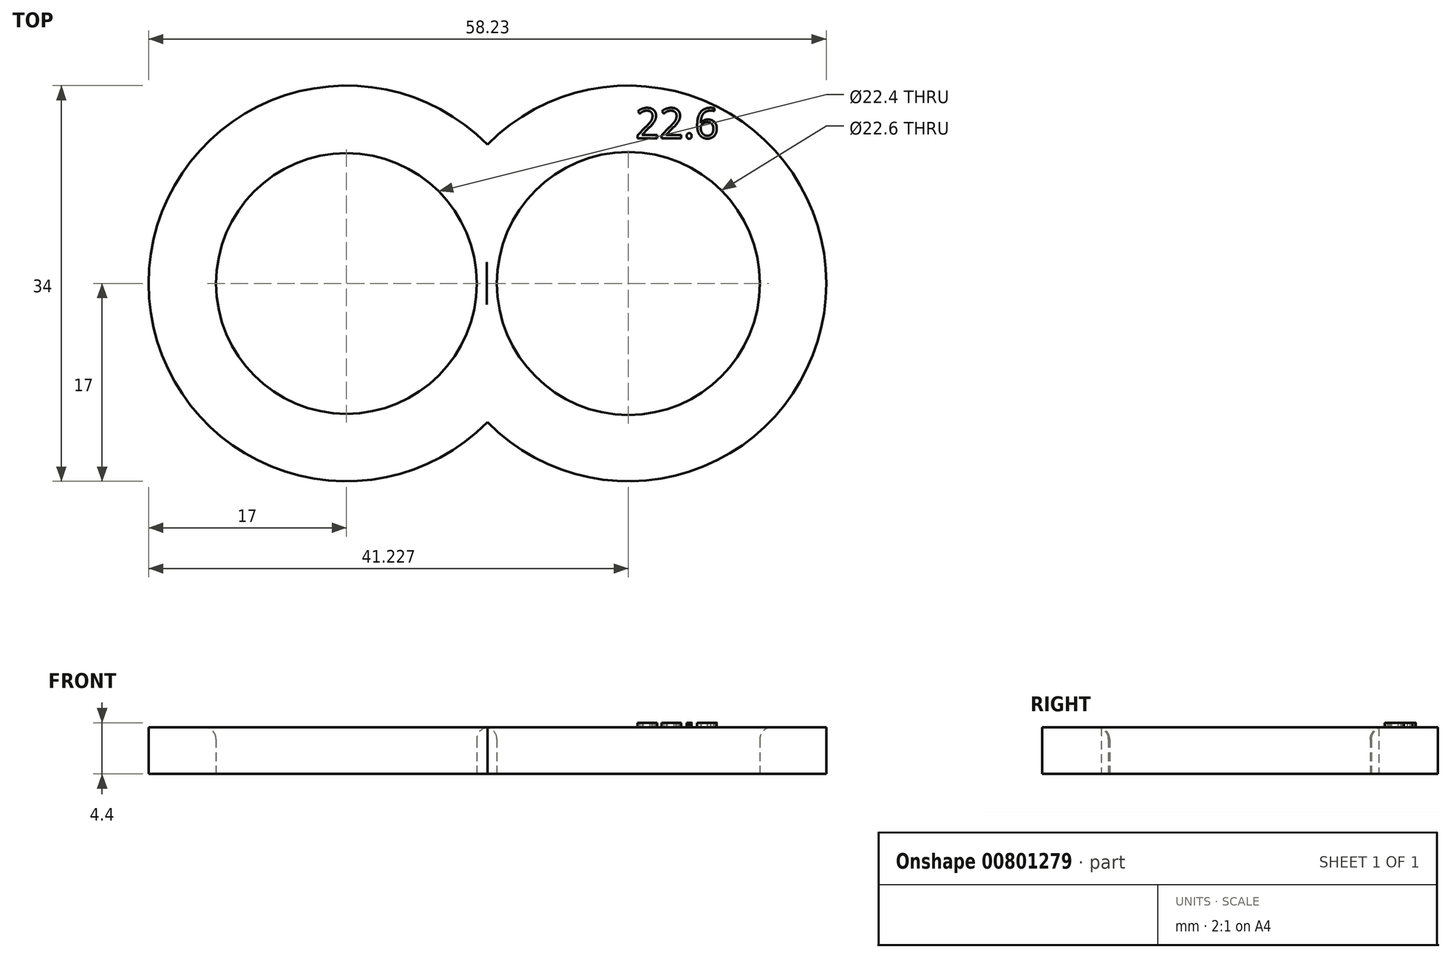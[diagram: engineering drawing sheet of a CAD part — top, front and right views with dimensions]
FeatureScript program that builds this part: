
annotation { "Feature Type Name" : "Feature", "Feature Type Description" : "" }
export const myFeature = defineFeature(function(context is Context, id is Id, definition is map)
    precondition{}
    {
        {
            var Q0;
            Q0=qCreatedBy(makeId("Top.planeOp"),FACE);
            var sketch = newSketch(context, id + "F0", { "sketchPlane" : qUnion([Q0])});
            skCircle(sketch, "E0", {"center": v(0, 0) * mm, "radius": 11.2 * mm});
            skCircle(sketch, "E1", {"center": v(0, 0) * mm, "radius": 17 * mm});
            skCircle(sketch, "E2", {"center": v(24.23, 0) * mm, "radius": 11.3 * mm});
            skCircle(sketch, "E3", {"center": v(24.23, 0) * mm, "radius": 17 * mm});
            skSolve(sketch);
        }
        {
            var Q0;
            {var subQ0=sQuery(id+"F0.wireOp",EDGE,"E3");var subQ1=sQuery(id+"F0.wireOp",EDGE,"E0");var subQ2=makeQuery(id+"F0.imprint","INTERSECT",VERTEX,{"disambiguationData":[OD(0.0)],"derivedFrom":[subQ1,subQ0]});Q0=makeQuery(id+"F0.imprint","IMPRINT",FACE,{"disambiguationData":[TD([[makeQuery(id+"F0.imprint","IMPRINT",EDGE,{"disambiguationData":[TD([[subQ2,-1.0]])],"derivedFrom":subQ1}),-1.0]])]});}
            var Q1;
            {var subQ0=sQuery(id+"F0.wireOp",EDGE,"E3");var subQ1=sQuery(id+"F0.wireOp",EDGE,"E0");var subQ2=makeQuery(id+"F0.imprint","INTERSECT",VERTEX,{"disambiguationData":[OD(0.0)],"derivedFrom":[subQ1,subQ0]});Q1=makeQuery(id+"F0.imprint","IMPRINT",FACE,{"disambiguationData":[TD([[makeQuery(id+"F0.imprint","IMPRINT",EDGE,{"disambiguationData":[TD([[subQ2,1.0]])],"derivedFrom":subQ1}),-1.0]])]});}
            var Q2;
            {var subQ0=sQuery(id+"F0.wireOp",EDGE,"E3");var subQ1=sQuery(id+"F0.wireOp",EDGE,"E0");var subQ2=makeQuery(id+"F0.imprint","INTERSECT",VERTEX,{"disambiguationData":[OD(1.0)],"derivedFrom":[subQ1,subQ0]});Q2=makeQuery(id+"F0.imprint","IMPRINT",FACE,{"disambiguationData":[TD([[makeQuery(id+"F0.imprint","IMPRINT",EDGE,{"disambiguationData":[TD([[subQ2,-1.0]])],"derivedFrom":subQ1}),-1.0]])]});}
            var Q3;
            {var subQ0=sQuery(id+"F0.wireOp",EDGE,"E3");var subQ1=sQuery(id+"F0.wireOp",EDGE,"E1");var subQ2=makeQuery(id+"F0.imprint","INTERSECT",VERTEX,{"disambiguationData":[OD(0.0)],"derivedFrom":[subQ1,subQ0]});Q3=makeQuery(id+"F0.imprint","IMPRINT",FACE,{"disambiguationData":[TD([[makeQuery(id+"F0.imprint","IMPRINT",EDGE,{"disambiguationData":[TD([[subQ2,1.0]])],"derivedFrom":subQ1}),-1.0]])]});}
            extrude(context, id + "F1", {"entities" : qUnion([Q0, Q1, Q2, Q3]), "depth" : 4 * mm});
        }
        {
            var Q0;
            Q0=makeQuery(id+"F1.opExtrude","CAP_EDGE",EDGE,{"disambiguationData":[OSD([sQuery(id+"F0.wireOp",EDGE,"E0")])],"isStart":false});
            var Q1;
            Q1=makeQuery(id+"F1.opExtrude","CAP_EDGE",EDGE,{"disambiguationData":[OSD([sQuery(id+"F0.wireOp",EDGE,"E2")])],"isStart":false});
            fillet(context, id + "F2", {"entities" : qUnion([Q0, Q1]), "radius" : 1 * mm, "tangentPropagation" : true, "allowEdgeOverflow" : false});
        }
        {
            var Q0;
            Q0=makeQuery(id+"F1.opExtrude","CAP_FACE",FACE,{"disambiguationData":[OSD([sQuery(id+"F0.wireOp",EDGE,"E0"),sQuery(id+"F0.wireOp",EDGE,"E1"),sQuery(id+"F0.wireOp",EDGE,"E2"),sQuery(id+"F0.wireOp",EDGE,"E3")])],"isStart":false});
            var sketch = newSketch(context, id + "F3", { "sketchPlane" : qUnion([Q0])});
            skText(sketch, "E4", { "text": "22.6\n", "fontName": "OpenSans-Regular.ttf"});
            const initialGuessF3  = {"E4": [0.02484, 0.01248, 1, 0, 0.0026]};
            skSetInitialGuess(sketch, initialGuessF3);
            skSolve(sketch);
        }
        {
            var Q0;
            Q0=qSketchRegion(id+"F3",true);
            var Q1;
            Q1=qConstructionFilter(qBodyType(qCreatedBy(id+"F3",EDGE),BodyType.WIRE),ConstructionObject.NO);
            extrude(context, id + "F4", {"entities" : qUnion([Q0]), "operationType" : NewBodyOperationType.ADD, "surfaceEntities" : qUnion([Q1]), "depth" : 0.4 * mm});
        }
    });
